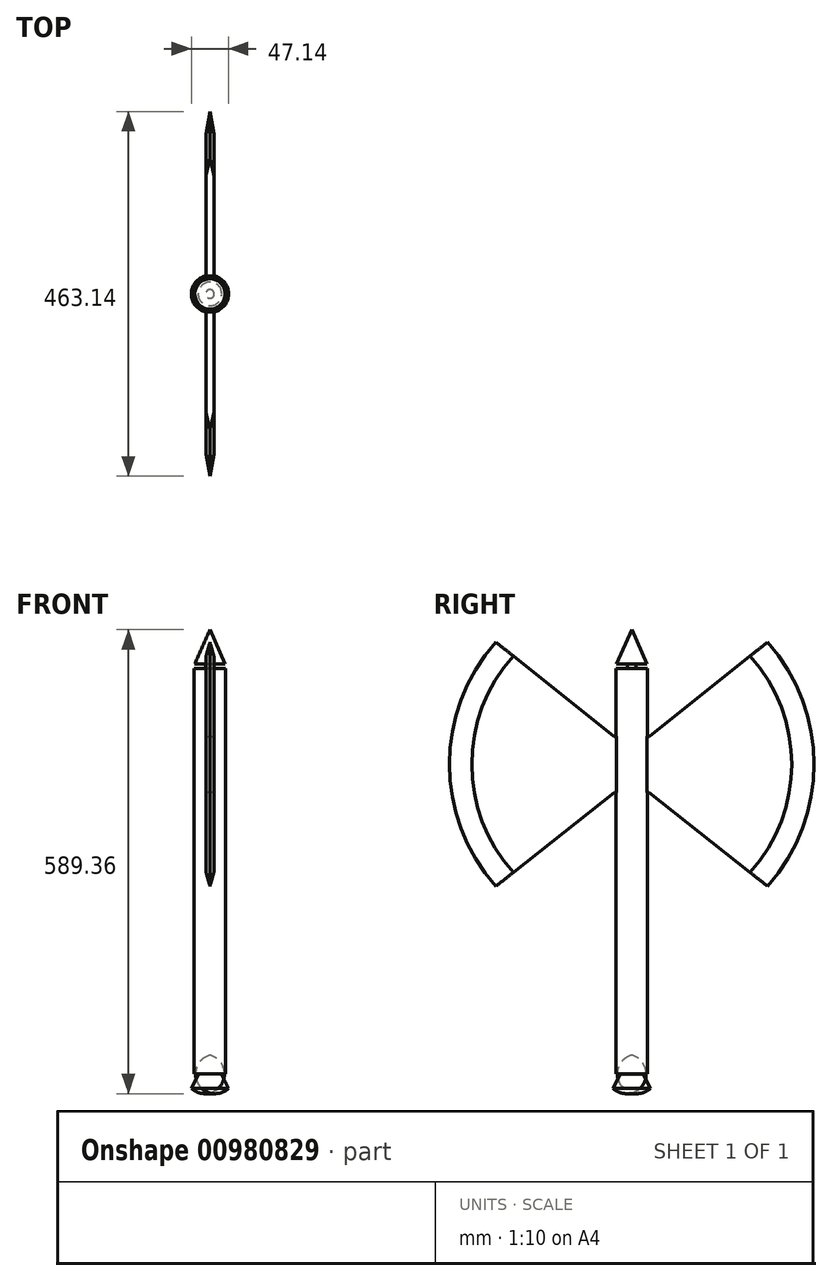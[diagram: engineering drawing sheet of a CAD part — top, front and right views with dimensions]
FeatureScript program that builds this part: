
annotation { "Feature Type Name" : "Feature", "Feature Type Description" : "" }
export const myFeature = defineFeature(function(context is Context, id is Id, definition is map)
    precondition{}
    {
        {
            var Q0;
            Q0=qCreatedBy(makeId("Top.planeOp"),FACE);
            var sketch = newSketch(context, id + "F0", { "sketchPlane" : qUnion([Q0])});
            skCircle(sketch, "E0", {"center": v(0, 0) * mm, "radius": 20 * mm});
            skSolve(sketch);
        }
        {
            var Q0;
            Q0=makeQuery(id+"F0.imprint","IMPRINT",FACE,{"disambiguationData":[TD([[makeQuery(id+"F0.imprint","IMPRINT",EDGE,{"derivedFrom":sQuery(id+"F0.wireOp",EDGE,"E0")}),1.0]])]});
            extrude(context, id + "F1", {"entities" : qUnion([Q0]), "depth" : 324 * mm, "offsetDistance" : 25 * mm, "hasSecondDirection" : true, "secondDirectionOppositeDirection" : true, "secondDirectionDepth" : 191 * mm});
        }
        {
            var Q0;
            Q0=qCreatedBy(makeId("Right.planeOp"),FACE);
            var sketch = newSketch(context, id + "F2", { "sketchPlane" : qUnion([Q0])});
            skLineSegment(sketch, "E1", {"start": v(21.85, 166.51) * mm, "end": v(172.58, 47.34) * mm});
            skLineSegment(sketch, "E2", {"start": v(22.43, 237.53) * mm, "end": v(172.58, 357.43) * mm});
            skArc(sketch, "E3", {"start": v(172.58, 47.34) * mm, "mid": v(231.57, 202.38) * mm, "end": v(172.58, 357.43) * mm});
            skLineSegment(sketch, "E4", {"start": v(22.43, 237.53) * mm, "end": v(9.84, 237.53) * mm});
            skLineSegment(sketch, "E5", {"start": v(9.84, 237.53) * mm, "end": v(9.84, 165.8) * mm});
            skLineSegment(sketch, "E6", {"start": v(9.84, 165.8) * mm, "end": v(21.85, 166.51) * mm});
            skSolve(sketch);
        }
        {
            var Q0;
            Q0=makeQuery(id+"F2.imprint","IMPRINT",FACE,{"disambiguationData":[TD([[makeQuery(id+"F2.imprint","IMPRINT",EDGE,{"derivedFrom":sQuery(id+"F2.wireOp",EDGE,"E1")}),1.0]])]});
            extrude(context, id + "F3", {"entities" : qUnion([Q0]), "operationType" : NewBodyOperationType.ADD, "depth" : 5 * mm, "offsetDistance" : 25 * mm});
        }
        {
            var Q0;
            Q0=makeQuery(id+"F3.opExtrude","CAP_EDGE",EDGE,{"disambiguationData":[OSD([sQuery(id+"F2.wireOp",EDGE,"E3")])],"isStart":false});
            chamfer(context, id + "F4", {"entities" : qUnion([Q0]), "chamferType" : ChamferType.OFFSET_ANGLE, "width" : 5 * mm, "oppositeDirection" : true, "angle" : 80 * degree, "tangentPropagation" : true});
        }
        {
            var Q0;
            Q0=makeQuery(id+"F1.opExtrude","SWEPT_BODY",BODY,{"disambiguationData":[OSD([sQuery(id+"F0.wireOp",EDGE,"E0")])]});
            var Q1;
            Q1=qCreatedBy(makeId("Right.planeOp"),FACE);
            mirror(context, id + "F5", {"operationType" : NewBodyOperationType.ADD, "entities" : qUnion([Q0]), "mirrorPlane" : qUnion([Q1])});
        }
        {
            var Q0;
            Q0=makeQuery(id+"F1.opExtrude","SWEPT_BODY",BODY,{"disambiguationData":[OSD([sQuery(id+"F0.wireOp",EDGE,"E0")])]});
            var Q1;
            Q1=qCreatedBy(makeId("Front.planeOp"),FACE);
            mirror(context, id + "F6", {"operationType" : NewBodyOperationType.ADD, "entities" : qUnion([Q0]), "mirrorPlane" : qUnion([Q1])});
        }
        {
            var Q0;
            Q0=qCreatedBy(makeId("Right.planeOp"),FACE);
            var sketch = newSketch(context, id + "F7", { "sketchPlane" : qUnion([Q0])});
            skLineSegment(sketch, "E7", {"start": v(5.5, 329.43) * mm, "end": v(19.35, 329.43) * mm});
            skLineSegment(sketch, "E8", {"start": v(19.35, 329.43) * mm, "end": v(0, 373.18) * mm});
            skLineSegment(sketch, "E9", {"start": v(0, 373.18) * mm, "end": v(0, 329.43) * mm});
            skLineSegment(sketch, "E10", {"start": v(0, 329.43) * mm, "end": v(0, 312.62) * mm});
            skLineSegment(sketch, "E11", {"start": v(0, 312.62) * mm, "end": v(5.5, 312.62) * mm});
            skLineSegment(sketch, "E12", {"start": v(5.5, 312.62) * mm, "end": v(5.5, 329.43) * mm});
            skSolve(sketch);
        }
        {
            var Q0;
            Q0=makeQuery(id+"F7.imprint","IMPRINT",FACE,{"disambiguationData":[TD([[makeQuery(id+"F7.imprint","IMPRINT",EDGE,{"derivedFrom":sQuery(id+"F7.wireOp",EDGE,"E7")}),1.0]])]});
            var Q1;
            Q1=sQuery(id+"F7.wireOp",EDGE,"E9");
            revolve(context, id + "F8", {"operationType" : NewBodyOperationType.ADD, "surfaceOperationType" : NewSurfaceOperationType.NEW, "entities" : qUnion([Q0]), "axis" : qUnion([Q1]), "revolveType" : RevolveType.FULL});
        }
        {
            var Q0;
            Q0=qCreatedBy(makeId("Right.planeOp"),FACE);
            var sketch = newSketch(context, id + "F9", { "sketchPlane" : qUnion([Q0])});
            skLineSegment(sketch, "E13", {"start": v(-15.05, -192.41) * mm, "end": v(-23.57, -209.45) * mm});
            skLineSegment(sketch, "E14", {"start": v(0, -193.28) * mm, "end": v(0, -209.45) * mm});
            skLineSegment(sketch, "E15", {"start": v(-15.05, -192.41) * mm, "end": v(-15.05, -187.7) * mm});
            skLineSegment(sketch, "E16", {"start": v(-15.05, -187.7) * mm, "end": v(0, -187.7) * mm});
            skLineSegment(sketch, "E17", {"start": v(0, -187.7) * mm, "end": v(0, -193.28) * mm});
            skLineSegment(sketch, "E18", {"start": v(0, -209.45) * mm, "end": v(0, -215.3) * mm});
            skArc(sketch, "E19", {"start": v(-23.57, -209.45) * mm, "mid": v(-12.55, -215.44) * mm, "end": v(0, -215.3) * mm});
            skSolve(sketch);
        }
        {
            var Q0;
            Q0=makeQuery(id+"F9.imprint","IMPRINT",FACE,{"disambiguationData":[TD([[makeQuery(id+"F9.imprint","IMPRINT",EDGE,{"derivedFrom":sQuery(id+"F9.wireOp",EDGE,"E13")}),1.0]])]});
            var Q1;
            Q1=sQuery(id+"F9.wireOp",EDGE,"E14");
            revolve(context, id + "F10", {"operationType" : NewBodyOperationType.ADD, "surfaceOperationType" : NewSurfaceOperationType.NEW, "entities" : qUnion([Q0]), "axis" : qUnion([Q1]), "revolveType" : RevolveType.FULL});
        }
    });
